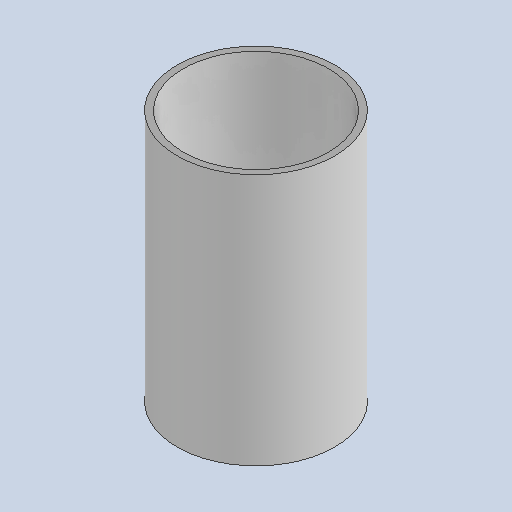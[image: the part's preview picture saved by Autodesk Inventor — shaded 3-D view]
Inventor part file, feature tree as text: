
AUTODESK INVENTOR PART (.ipt)
format: ipt  version: 2025 (Build 290162010, 162A)  size: 92,672 bytes
history: native  units: mm
features: extrude x1, sketch x1
ambient origin geometry x8: Origin, YZ Plane, XZ Plane, XY Plane, X Axis, Y Axis, Z Axis, Center Point
bodies: Solid1 (feature_tree)
feature tree (2):
  extrude  "Extrusion1"  Depth=200.0mm
  sketch  "Sketch1"  dims[d0=125.0mm d1=5.0mm d2=200.0mm d3=0.0mm]
